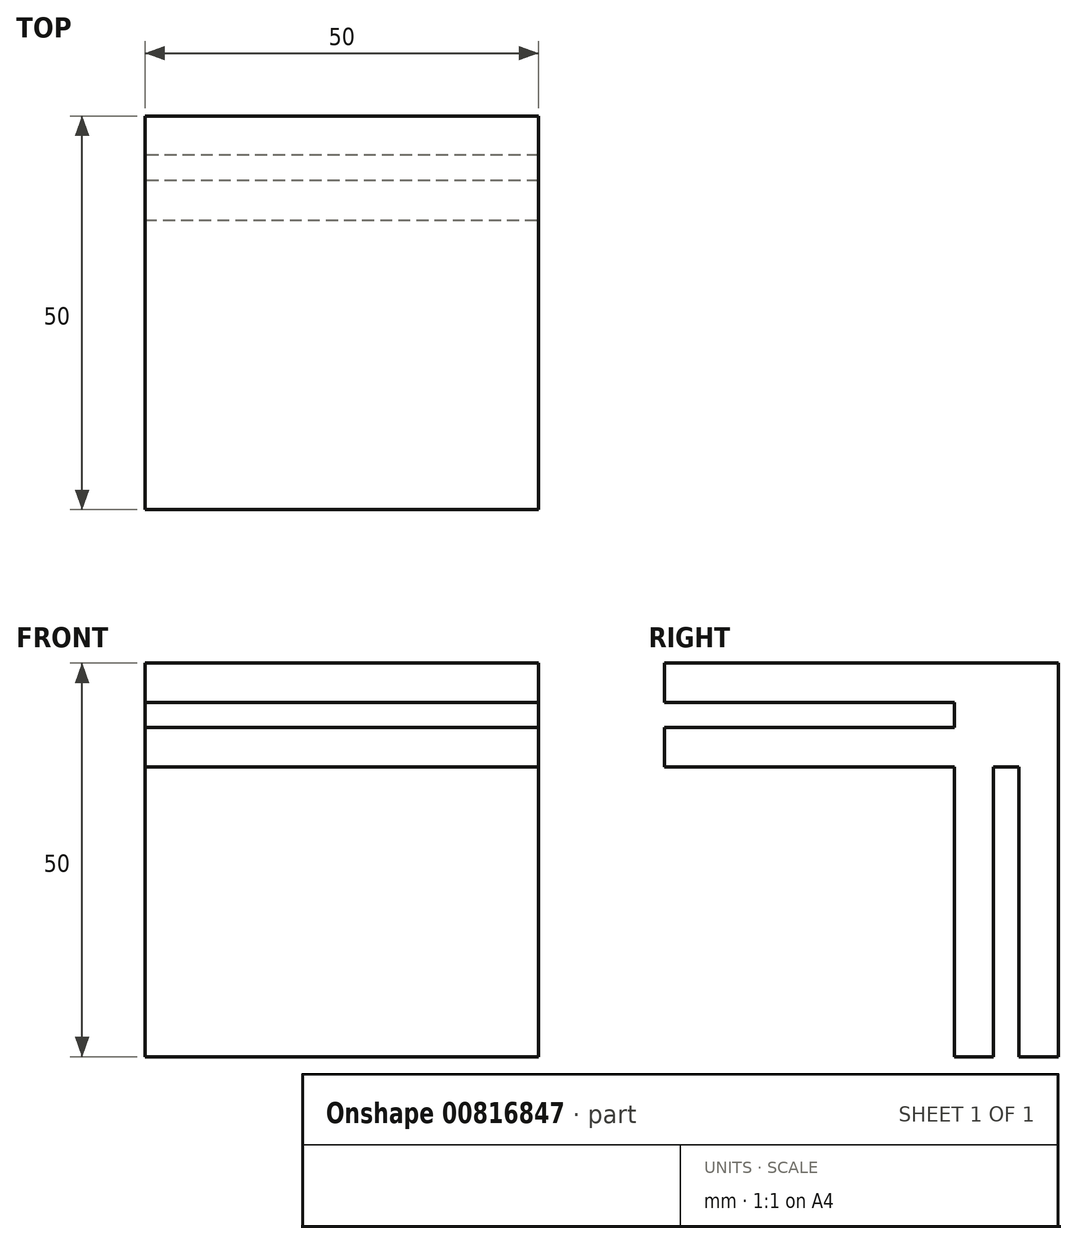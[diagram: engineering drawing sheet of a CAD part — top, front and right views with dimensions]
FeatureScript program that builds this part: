
annotation { "Feature Type Name" : "Feature", "Feature Type Description" : "" }
export const myFeature = defineFeature(function(context is Context, id is Id, definition is map)
    precondition{}
    {
        {
            var Q0;
            Q0=qCreatedBy(makeId("Top.planeOp"),FACE);
            var sketch = newSketch(context, id + "F0", { "sketchPlane" : qUnion([Q0])});
            skLineSegment(sketch, "E0.bottom", {"start": v(25, -25) * mm, "end": v(-25, -25) * mm});
            skLineSegment(sketch, "E0.top", {"start": v(25, 25) * mm, "end": v(-25, 25) * mm});
            skLineSegment(sketch, "E0.left", {"start": v(25, -25) * mm, "end": v(25, 25) * mm});
            skLineSegment(sketch, "E0.right", {"start": v(-25, -25) * mm, "end": v(-25, 25) * mm});
            skPoint(sketch, "E0.middle", {"position": v(0, 0) * mm});
            skSolve(sketch);
        }
        {
            var Q0;
            Q0=qSketchRegion(id+"F0",true);
            extrude(context, id + "F1", {"entities" : qUnion([Q0]), "depth" : 5 * mm, "offsetDistance" : 25 * mm});
        }
        {
            var Q0;
            Q0=makeQuery(id+"F1.opExtrude","SWEPT_FACE",FACE,{"disambiguationData":[OSD([sQuery(id+"F0.wireOp",EDGE,"E0.right")])]});
            var sketch = newSketch(context, id + "F2", { "sketchPlane" : qUnion([Q0])});
            skLineSegment(sketch, "E1.bottom", {"start": v(-25, 5) * mm, "end": v(-20, 5) * mm});
            skLineSegment(sketch, "E1.top", {"start": v(-25, -45) * mm, "end": v(-20, -45) * mm});
            skLineSegment(sketch, "E1.left", {"start": v(-25, 5) * mm, "end": v(-25, -45) * mm});
            skLineSegment(sketch, "E1.right", {"start": v(-20, 5) * mm, "end": v(-20, -45) * mm});
            skLineSegment(sketch, "E2.bottom", {"start": v(-16.8, 5) * mm, "end": v(-11.8, 5) * mm});
            skLineSegment(sketch, "E2.top", {"start": v(-16.8, -45) * mm, "end": v(-11.8, -45) * mm});
            skLineSegment(sketch, "E2.left", {"start": v(-16.8, 5) * mm, "end": v(-16.8, -45) * mm});
            skLineSegment(sketch, "E2.right", {"start": v(-11.8, 5) * mm, "end": v(-11.8, -45) * mm});
            skLineSegment(sketch, "E3", {"start": v(-22.5, -45) * mm, "end": v(-7.39, -45) * mm, "construction": true});
            skSolve(sketch);
        }
        {
            var Q0;
            Q0=qSketchRegion(id+"F2",true);
            var Q1;
            Q1=qSketchRegion(id+"F8mCDAmMXpJjheD_3",true);
            var Q2;
            Q2=makeQuery(id+"F1.opExtrude","SWEPT_FACE",FACE,{"disambiguationData":[OSD([sQuery(id+"F0.wireOp",EDGE,"E0.left")])]});
            extrude(context, id + "F3", {"entities" : qUnion([Q0, Q1]), "operationType" : NewBodyOperationType.ADD, "endBound" : BoundingType.UP_TO_SURFACE, "oppositeDirection" : true, "depth" : 25 * mm, "endBoundEntityFace" : qUnion([Q2]), "offsetDistance" : 25 * mm});
        }
        {
            var Q0;
            Q0=makeQuery(id+"F3.opExtrude","SWEPT_FACE",FACE,{"disambiguationData":[OSD([sQuery(id+"F2.wireOp",EDGE,"E2.right")])]});
            var sketch = newSketch(context, id + "F4", { "sketchPlane" : qUnion([Q0])});
            skLineSegment(sketch, "E4.bottom", {"start": v(-25, -3.2) * mm, "end": v(25, -3.2) * mm});
            skLineSegment(sketch, "E4.top", {"start": v(-25, -8.2) * mm, "end": v(25, -8.2) * mm});
            skLineSegment(sketch, "E4.left", {"start": v(-25, -3.2) * mm, "end": v(-25, -8.2) * mm});
            skLineSegment(sketch, "E4.right", {"start": v(25, -3.2) * mm, "end": v(25, -8.2) * mm});
            skSolve(sketch);
        }
        {
            var Q0;
            Q0=qSketchRegion(id+"F4",true);
            var Q1;
            Q1=makeQuery(id+"F1.opExtrude","SWEPT_FACE",FACE,{"disambiguationData":[OSD([sQuery(id+"F0.wireOp",EDGE,"E0.bottom")])]});
            extrude(context, id + "F5", {"entities" : qUnion([Q0]), "operationType" : NewBodyOperationType.ADD, "endBound" : BoundingType.UP_TO_SURFACE, "depth" : 25 * mm, "endBoundEntityFace" : qUnion([Q1]), "offsetDistance" : 25 * mm});
        }
        {
            var Q0;
            Q0=makeQuery(id+"F5.boolean.opBoolean","MERGE",FACE,{"derivedFrom":[makeQuery(id+"F3.boolean.opBoolean","MERGE",FACE,{"derivedFrom":[makeQuery(id+"F1.opExtrude","SWEPT_FACE",FACE,{"disambiguationData":[OSD([sQuery(id+"F0.wireOp",EDGE,"E0.right")])]}),makeQuery(id+"F3.opExtrude","CAP_FACE",FACE,{"disambiguationData":[OSD([sQuery(id+"F2.wireOp",EDGE,"E1.bottom"),sQuery(id+"F2.wireOp",EDGE,"E1.top"),sQuery(id+"F2.wireOp",EDGE,"E1.left"),sQuery(id+"F2.wireOp",EDGE,"E1.right")])],"isStart":true}),makeQuery(id+"F3.opExtrude","CAP_FACE",FACE,{"disambiguationData":[OSD([sQuery(id+"F2.wireOp",EDGE,"E2.bottom"),sQuery(id+"F2.wireOp",EDGE,"E2.top"),sQuery(id+"F2.wireOp",EDGE,"E2.left"),sQuery(id+"F2.wireOp",EDGE,"E2.right")])],"isStart":true})]}),makeQuery(id+"F5.opExtrude","SWEPT_FACE",FACE,{"disambiguationData":[OSD([sQuery(id+"F4.wireOp",EDGE,"E4.left")])]})]});
            var sketch = newSketch(context, id + "F6", { "sketchPlane" : qUnion([Q0])});
            skLineSegment(sketch, "E5.bottom", {"start": v(-16.8, -8.2) * mm, "end": v(-20, -8.2) * mm});
            skLineSegment(sketch, "E5.top", {"start": v(-16.8, 0) * mm, "end": v(-20, 0) * mm});
            skLineSegment(sketch, "E5.left", {"start": v(-16.8, -8.2) * mm, "end": v(-16.8, 0) * mm});
            skLineSegment(sketch, "E5.right", {"start": v(-20, -8.2) * mm, "end": v(-20, 0) * mm});
            skSolve(sketch);
        }
        {
            var Q0;
            Q0=qSketchRegion(id+"F6",true);
            var Q1;
            Q1=makeQuery(id+"F5.boolean.opBoolean","MERGE",FACE,{"derivedFrom":[makeQuery(id+"F3.boolean.opBoolean","MERGE",FACE,{"derivedFrom":[makeQuery(id+"F1.opExtrude","SWEPT_FACE",FACE,{"disambiguationData":[OSD([sQuery(id+"F0.wireOp",EDGE,"E0.left")])]}),makeQuery(id+"F3.opExtrude","CAP_FACE",FACE,{"disambiguationData":[OSD([sQuery(id+"F2.wireOp",EDGE,"E1.bottom"),sQuery(id+"F2.wireOp",EDGE,"E1.top"),sQuery(id+"F2.wireOp",EDGE,"E1.left"),sQuery(id+"F2.wireOp",EDGE,"E1.right")])],"isStart":false}),makeQuery(id+"F3.opExtrude","CAP_FACE",FACE,{"disambiguationData":[OSD([sQuery(id+"F2.wireOp",EDGE,"E2.bottom"),sQuery(id+"F2.wireOp",EDGE,"E2.top"),sQuery(id+"F2.wireOp",EDGE,"E2.left"),sQuery(id+"F2.wireOp",EDGE,"E2.right")])],"isStart":false})]}),makeQuery(id+"F5.opExtrude","SWEPT_FACE",FACE,{"disambiguationData":[OSD([sQuery(id+"F4.wireOp",EDGE,"E4.right")])]})]});
            extrude(context, id + "F7", {"entities" : qUnion([Q0]), "operationType" : NewBodyOperationType.ADD, "endBound" : BoundingType.UP_TO_SURFACE, "oppositeDirection" : true, "depth" : 25 * mm, "endBoundEntityFace" : qUnion([Q1]), "offsetDistance" : 25 * mm});
        }
    });
